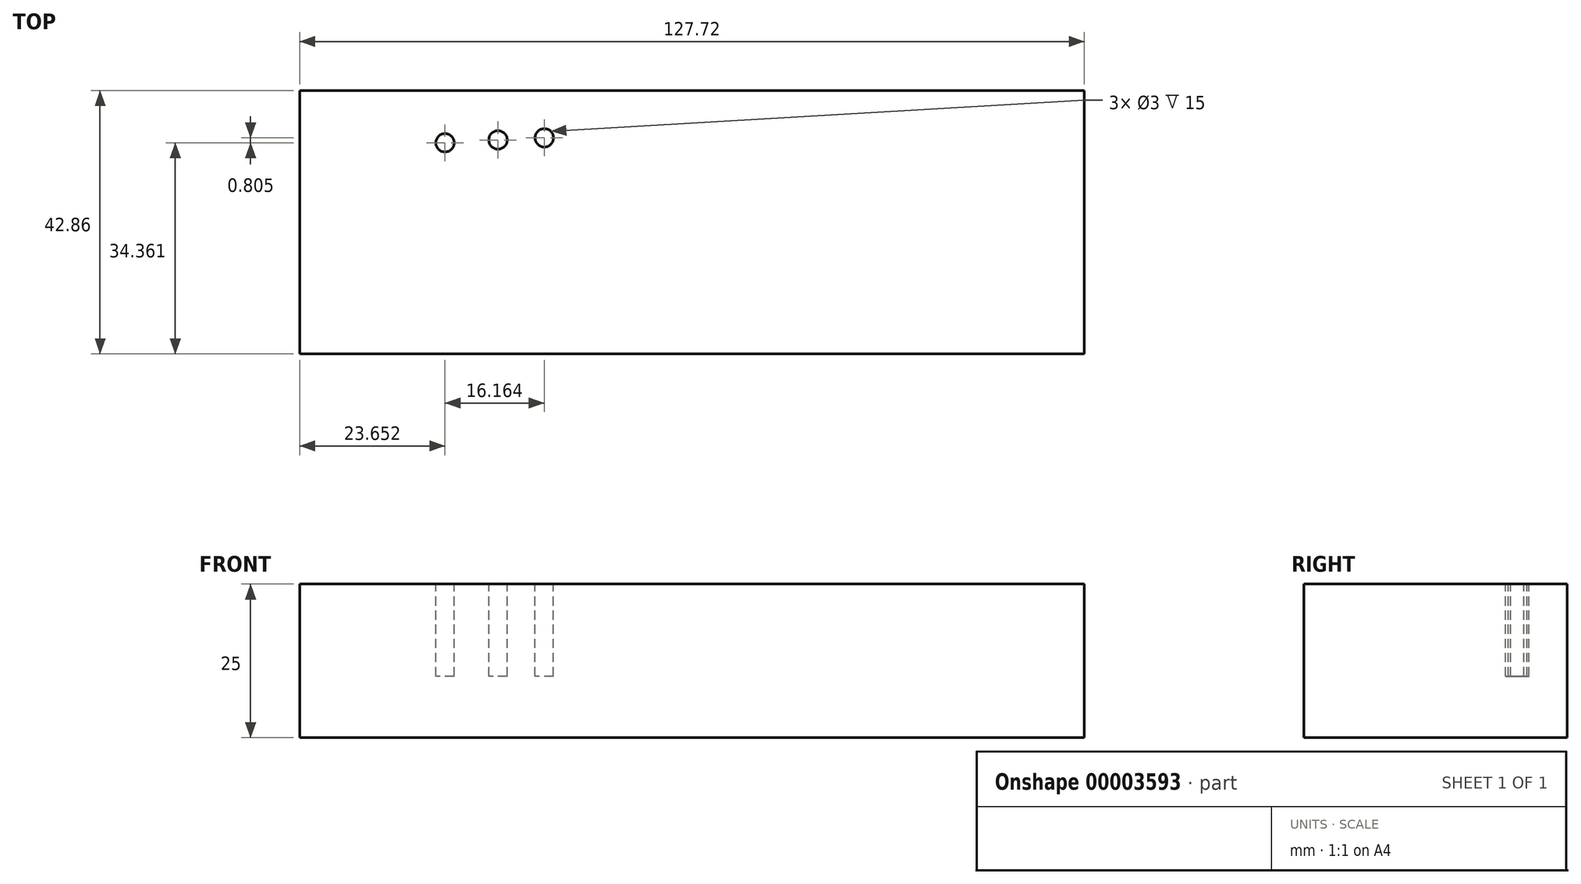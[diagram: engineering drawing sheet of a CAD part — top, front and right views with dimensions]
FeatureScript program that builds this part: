
annotation { "Feature Type Name" : "Feature", "Feature Type Description" : "" }
export const myFeature = defineFeature(function(context is Context, id is Id, definition is map)
    precondition{}
    {
        {
            var Q0;
            Q0=qCreatedBy(makeId("Top.planeOp"),FACE);
            var sketch = newSketch(context, id + "F0", { "sketchPlane" : qUnion([Q0])});
            skLineSegment(sketch, "E0.rect.bottom", {"start": v(-63.86, -21.43) * mm, "end": v(63.86, -21.43) * mm});
            skLineSegment(sketch, "E0.rect.top", {"start": v(-63.86, 21.43) * mm, "end": v(63.86, 21.43) * mm});
            skLineSegment(sketch, "E0.rect.left", {"start": v(-63.86, -21.43) * mm, "end": v(-63.86, 21.43) * mm});
            skLineSegment(sketch, "E0.rect.right", {"start": v(63.86, -21.43) * mm, "end": v(63.86, 21.43) * mm});
            skPoint(sketch, "E0.rect.middle", {"position": v(0, 0) * mm});
            skSolve(sketch);
        }
        {
            var Q0;
            Q0 = qSketchRegion(id + "F0", true);
            extrude(context, id + "F1", {"entities" : qUnion([Q0]), "depth" : 25 * mm});
        }
        {
            var Q0;
            Q0=makeQuery(id+"F1.opExtrude","CAP_FACE",FACE,{"disambiguationData":[OSD([sQuery(id+"F0.wireOp",EDGE,"E0.rect.bottom"),sQuery(id+"F0.wireOp",EDGE,"E0.rect.top"),sQuery(id+"F0.wireOp",EDGE,"E0.rect.left"),sQuery(id+"F0.wireOp",EDGE,"E0.rect.right")])],"isStart":false});
            var sketch = newSketch(context, id + "F2", { "sketchPlane" : qUnion([Q0])});
            skCircle(sketch, "E1", {"center": v(-40.2, 12.93) * mm, "radius": 1.5 * mm});
            skCircle(sketch, "E2", {"center": v(-31.58, 13.4) * mm, "radius": 1.5 * mm});
            skCircle(sketch, "E3", {"center": v(-24.04, 13.74) * mm, "radius": 1.5 * mm});
            skSolve(sketch);
        }
        {
            var Q0;
            Q0 = qSketchRegion(id + "F2", true);
            extrude(context, id + "F3", {"entities" : qUnion([Q0]), "operationType" : NewBodyOperationType.REMOVE, "oppositeDirection" : true, "depth" : 15 * mm});
        }
    });
